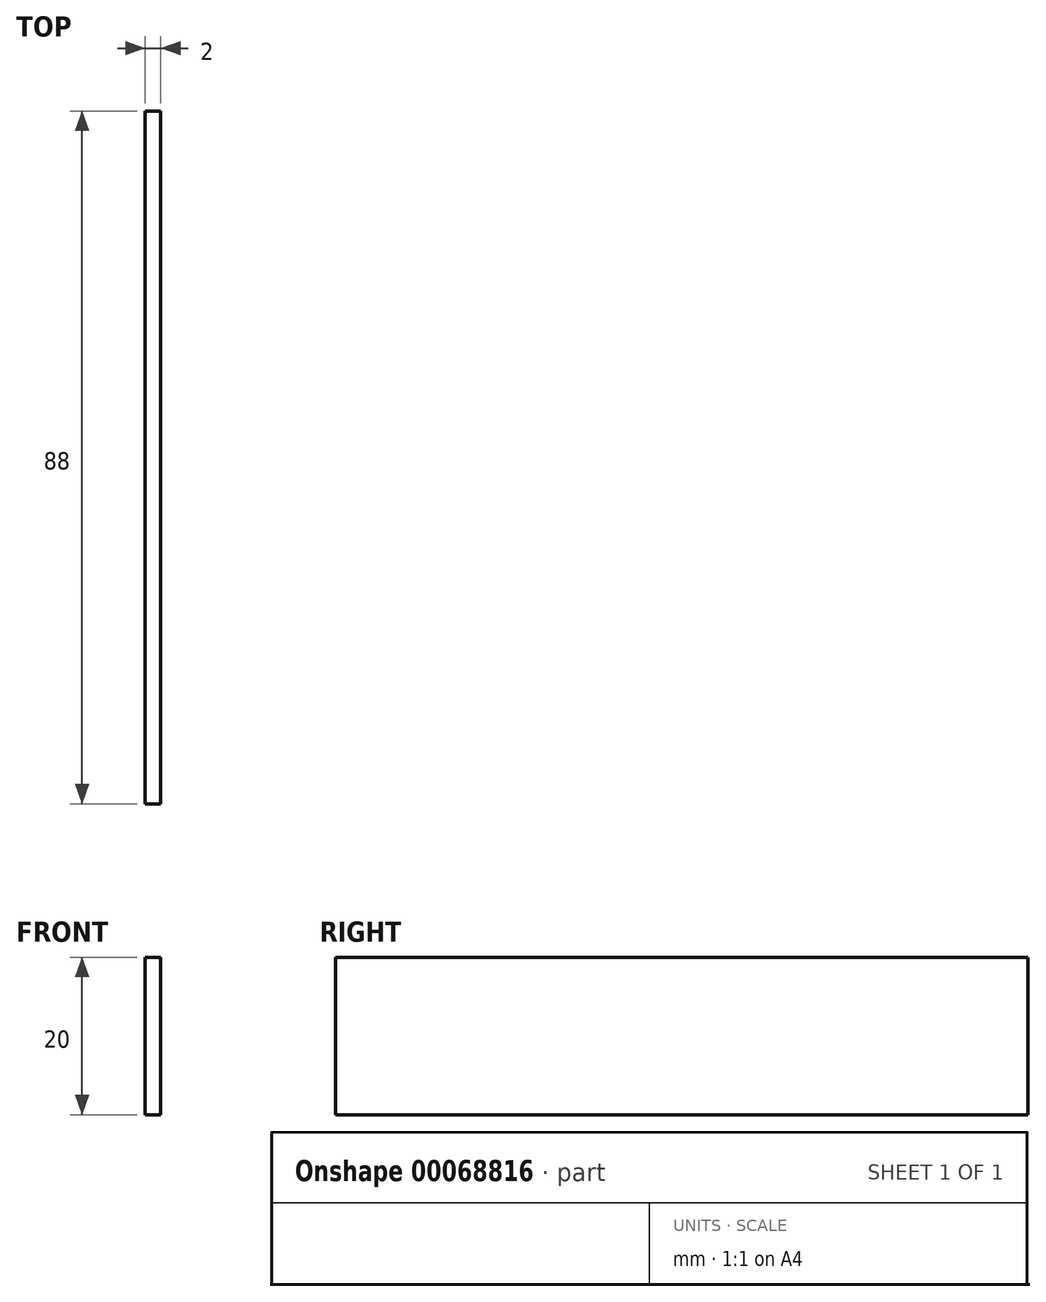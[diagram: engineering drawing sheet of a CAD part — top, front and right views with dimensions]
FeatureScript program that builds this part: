
annotation { "Feature Type Name" : "Feature", "Feature Type Description" : "" }
export const myFeature = defineFeature(function(context is Context, id is Id, definition is map)
    precondition{}
    {
        {
            var Q0;
            Q0=qCreatedBy(makeId("Right.planeOp"),FACE);
            var sketch = newSketch(context, id + "F0", { "sketchPlane" : qUnion([Q0])});
            skLineSegment(sketch, "E0.bottom", {"start": v(0, 0) * mm, "end": v(88, 0) * mm});
            skLineSegment(sketch, "E0.top", {"start": v(0, 20) * mm, "end": v(88, 20) * mm});
            skLineSegment(sketch, "E0.left", {"start": v(0, 0) * mm, "end": v(0, 20) * mm});
            skLineSegment(sketch, "E0.right", {"start": v(88, 0) * mm, "end": v(88, 20) * mm});
            skSolve(sketch);
        }
        {
            var Q0;
            Q0 = qSketchRegion(id + "F0", true);
            extrude(context, id + "F1", {"entities" : qUnion([Q0]), "depth" : 2 * mm});
        }
    });
